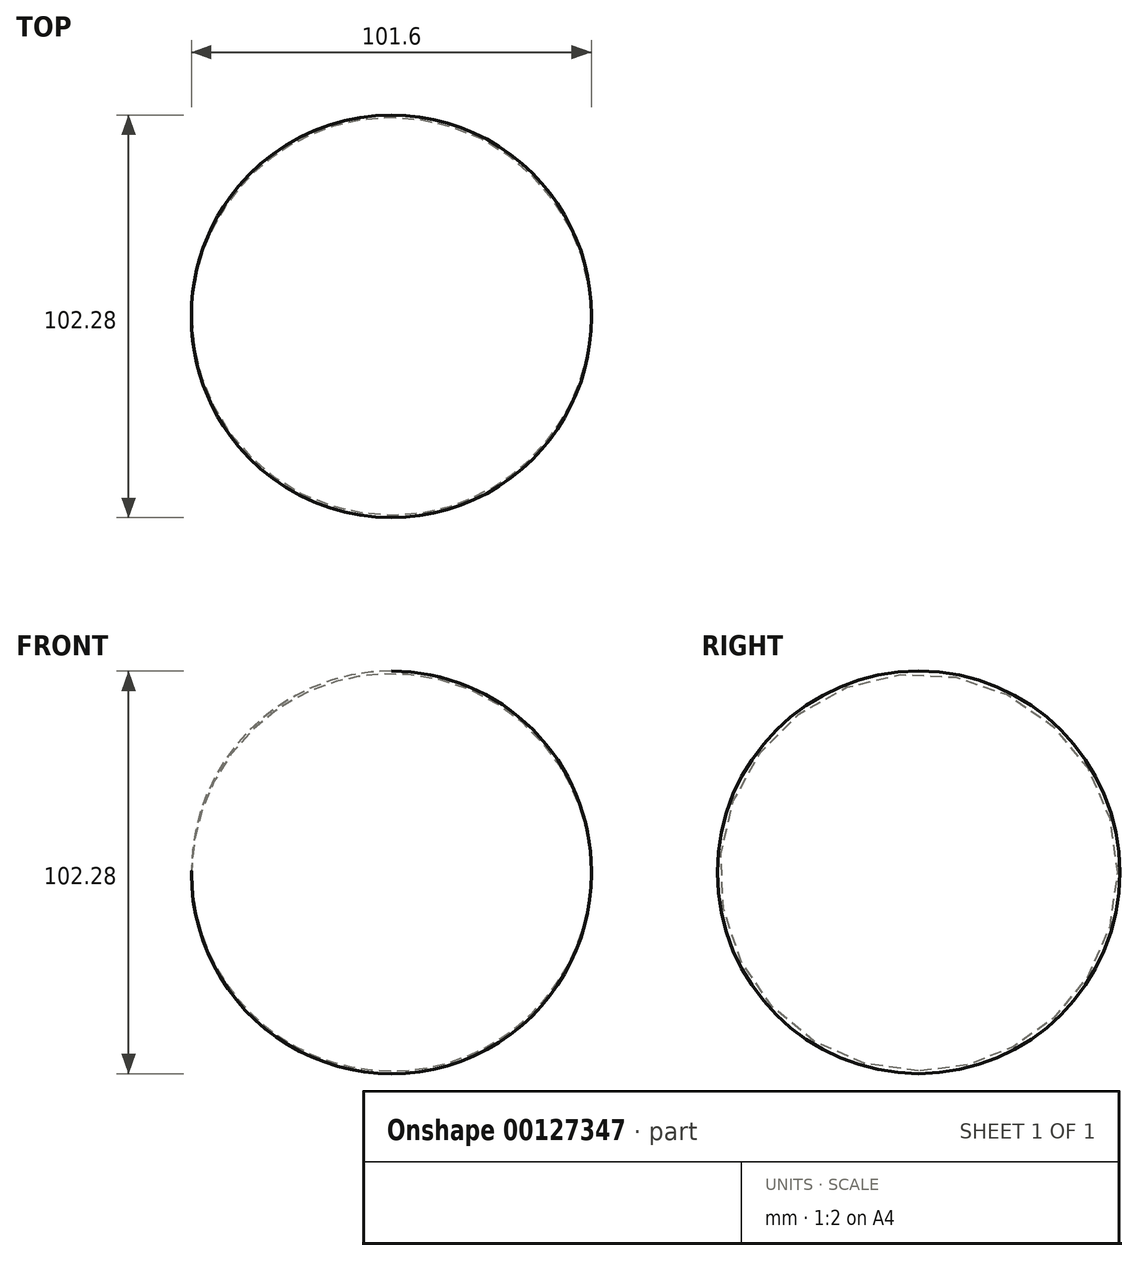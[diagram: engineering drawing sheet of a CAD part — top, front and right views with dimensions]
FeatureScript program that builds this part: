
annotation { "Feature Type Name" : "Feature", "Feature Type Description" : "" }
export const myFeature = defineFeature(function(context is Context, id is Id, definition is map)
    precondition{}
    {
        {
            var Q0;
            Q0=qCreatedBy(makeId("Front.planeOp"),FACE);
            var sketch = newSketch(context, id + "F0", { "sketchPlane" : qUnion([Q0])});
            skLineSegment(sketch, "E0", {"start": v(0, 0) * mm, "end": v(101.6, 0) * mm});
            skArc(sketch, "E1", {"start": v(101.6, 0) * mm, "mid": v(50.8, 50.47) * mm, "end": v(0, 0) * mm});
            skSolve(sketch);
        }
        {
            var Q0;
            Q0 = qSketchRegion(id + "F0", true);
            var Q1;
            Q1=sQuery(id+"F0.wireOp",EDGE,"E0");
            revolve(context, id + "F1", {"entities" : qUnion([Q0]), "axis" : qUnion([Q1]), "revolveType" : RevolveType.FULL});
        }
    });
